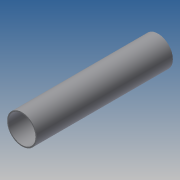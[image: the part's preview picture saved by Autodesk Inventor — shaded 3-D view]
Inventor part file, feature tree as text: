
AUTODESK INVENTOR PART (.ipt)
format: ipt  version: 2014 SP1 (Build 180222100, 222)  size: 76,800 bytes
history: native  units: in
note: dims shown in document units (in); Inventor stores cm internally (conversion verified against a paired STEP export)
features: extrude x1, sketch x1
ambient origin geometry x8: Origin, YZ Plane, XZ Plane, XY Plane, X Axis, Y Axis, Z Axis, Center Point
bodies: Solid1 (feature_tree)
feature tree (2):
  extrude  "Extrusion1"  Depth=19.685in
  sketch  "Sketch1"  dims[d0=3.937in d1=0.175in d2=19.685in d3=0.0in]
